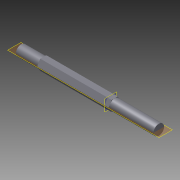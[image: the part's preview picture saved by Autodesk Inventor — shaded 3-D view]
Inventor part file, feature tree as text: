
AUTODESK INVENTOR PART (.ipt)
format: ipt  version: 2012 (Build 160160000, 160)  size: 162,304 bytes
history: native  units: in
note: dims shown in document units (in); Inventor stores cm internally (conversion verified against a paired STEP export)
features: other x6, plane x4, extrude x4, sketch x4, revolve x1
ambient origin geometry x6: Origin, XZ Plane, XY Plane, X Axis, Y Axis, Z Axis
bodies: Solid1 (feature_tree)
feature tree (19):
  revolve  "Revolution1"  [1 undecoded]
  other  "Alias Freeform1"
  other  "N-Side1"
  plane  "Work Plane1"
  plane  "Work Plane2"
  extrude  "Extrusion1"  Depth=0.25in
  plane  "Work Plane3"
  extrude  "Extrusion2"  [1 undecoded]
  plane  "Work Plane4"
  extrude  "Extrusion3"  Depth=0.23in
  extrude  "Extrusion4"  Depth=0.03in TaperAngle=0.0deg
  other  "Start Plane"
  other  "Origin point"
  other  "Main Sketch"
  other  "iFeature1:1"
  sketch  "Sketch3"  dims[d0=0.0in d1=0.0in d2=0.0in d3=0.25in]
  sketch  "Sketch4"  dims[d4=0.2887in d5=0.25in]
  sketch  "Sketch5"  dims[d6=0.0in d7=-2.13in]
  sketch  "Sketch6"  dims[d8=-0.61in d9=0.23in d10=0.03in d11=0.0in d12=0.16in d13=0.23in d14=0.03in d15=0.0in d16=-0.71in d17=0.23in d18=0.03in d19=0.0in d20=0.23in d21=0.03in d22=0.0in]
note: 2 required parameter values undecoded (feature->parameter linkage not recoverable at this tier; creation-order binding heuristic only, values carry confidence <= 0.55)